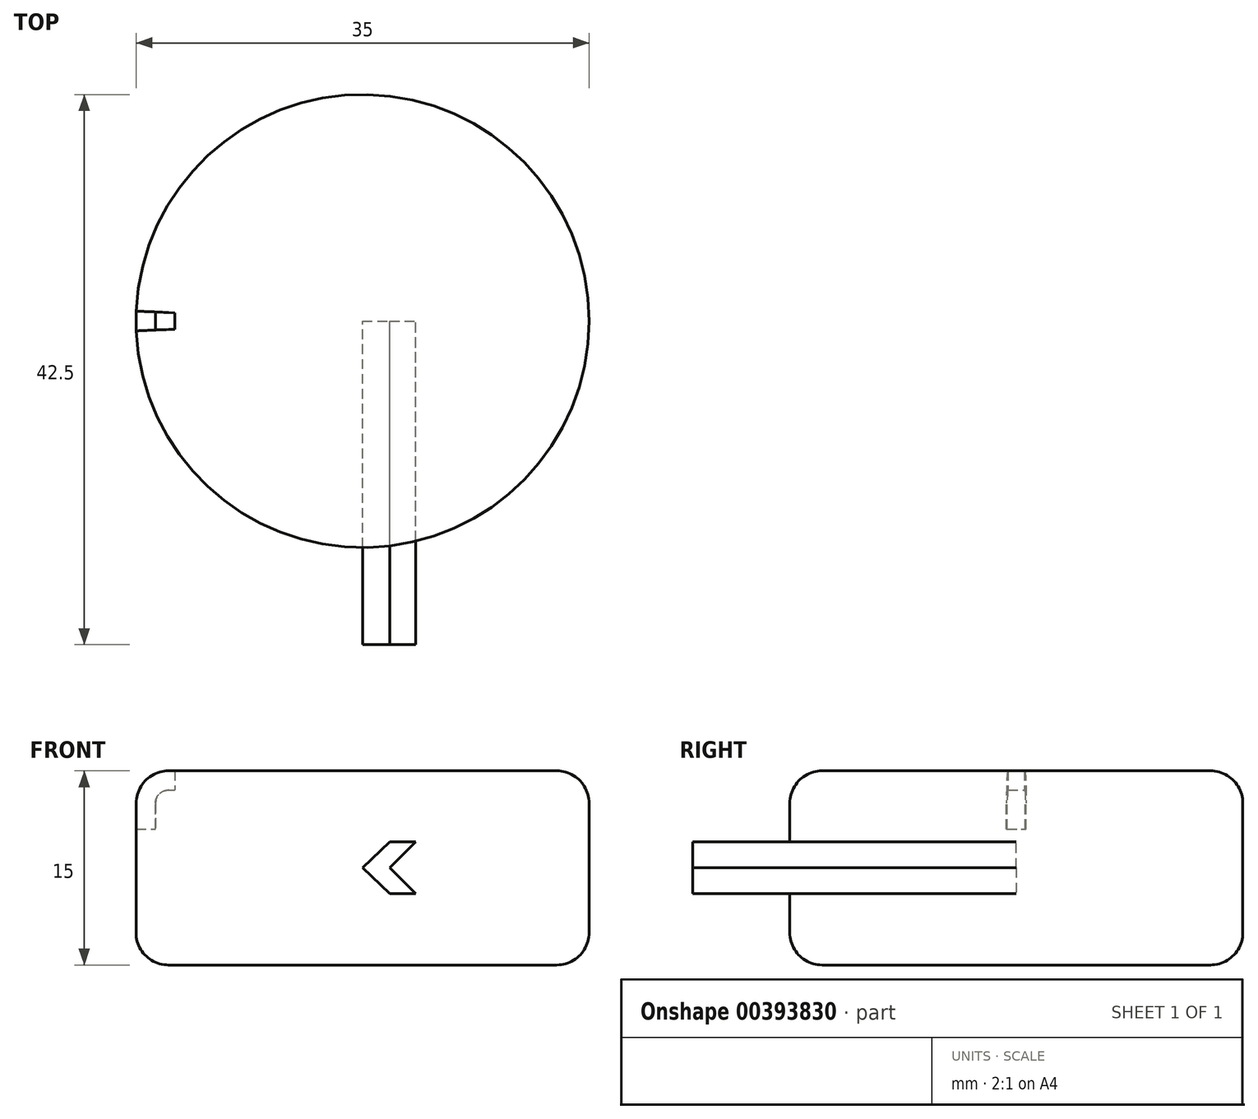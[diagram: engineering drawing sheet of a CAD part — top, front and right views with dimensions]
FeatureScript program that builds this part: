
annotation { "Feature Type Name" : "Feature", "Feature Type Description" : "" }
export const myFeature = defineFeature(function(context is Context, id is Id, definition is map)
    precondition{}
    {
        {
            var Q0;
            Q0=qCreatedBy(makeId("Front.planeOp"),FACE);
            var sketch = newSketch(context, id + "F0", { "sketchPlane" : qUnion([Q0])});
            skLineSegment(sketch, "E0", {"start": v(-38.31, 0) * mm, "end": v(38.96, 0) * mm, "construction": true});
            skLineSegment(sketch, "E1", {"start": v(0, 21.6) * mm, "end": v(0, -24.2) * mm, "construction": true});
            skLineSegment(sketch, "E2.bottom", {"start": v(0, 7.5) * mm, "end": v(-17.5, 7.5) * mm});
            skLineSegment(sketch, "E2.top", {"start": v(0, -7.5) * mm, "end": v(-17.5, -7.5) * mm});
            skLineSegment(sketch, "E2.right", {"start": v(-17.5, 7.5) * mm, "end": v(-17.5, -7.5) * mm});
            skPoint(sketch, "E2.middle", {"position": v(0, 0) * mm});
            skPoint(sketch, "E3.orphan", {"position": v(17.5, 7.5) * mm});
            skPoint(sketch, "E4.orphan", {"position": v(17.5, -7.5) * mm});
            skLineSegment(sketch, "E5", {"start": v(0, 7.5) * mm, "end": v(0, -7.5) * mm});
            skSolve(sketch);
        }
        {
            var Q0;
            Q0=makeQuery(id+"F0.imprint","IMPRINT",FACE,{"disambiguationData":[TD([[makeQuery(id+"F0.imprint","IMPRINT",EDGE,{"derivedFrom":sQuery(id+"F0.wireOp",EDGE,"E2.bottom")}),1.0]])]});
            var Q1;
            Q1=sQuery(id+"F0.wireOp",EDGE,"E5");
            revolve(context, id + "F1", {"entities" : qUnion([Q0]), "axis" : qUnion([Q1]), "revolveType" : RevolveType.FULL});
        }
        {
            var Q0;
            Q0=makeQuery(id+"F1.opRevolve","SWEPT_EDGE",EDGE,{"disambiguationData":[OSD([sQuery(id+"F0.wireOp",EDGE,"E2.bottom"),sQuery(id+"F0.wireOp",EDGE,"E2.right")])]});
            var Q1;
            Q1=makeQuery(id+"F1.opRevolve","SWEPT_EDGE",EDGE,{"disambiguationData":[OSD([sQuery(id+"F0.wireOp",EDGE,"E2.top"),sQuery(id+"F0.wireOp",EDGE,"E2.right")])]});
            fillet(context, id + "F2", {"entities" : qUnion([Q0, Q1]), "radius" : 2.5 * mm, "tangentPropagation" : true, "allowEdgeOverflow" : false});
        }
        {
            var Q0;
            Q0=qCreatedBy(makeId("Front.planeOp"),FACE);
            var sketch = newSketch(context, id + "F3", { "sketchPlane" : qUnion([Q0])});
            skLineSegment(sketch, "E6", {"start": v(-39.64, 0) * mm, "end": v(41.28, 0) * mm, "construction": true});
            skLineSegment(sketch, "E7", {"start": v(0, 20.88) * mm, "end": v(0, -28.83) * mm, "construction": true});
            skLineSegment(sketch, "E8", {"start": v(-15, 7.5) * mm, "end": v(15, 7.5) * mm});
            skArc(sketch, "E9", {"start": v(-15, 7.5) * mm, "mid": v(-16.77, 6.77) * mm, "end": v(-17.5, 5) * mm});
            skArc(sketch, "E10", {"start": v(17.5, 5) * mm, "mid": v(16.77, 6.77) * mm, "end": v(15, 7.5) * mm});
            skLineSegment(sketch, "E11", {"start": v(17.5, 5) * mm, "end": v(17.5, -5) * mm});
            skLineSegment(sketch, "E12", {"start": v(-17.5, -5) * mm, "end": v(-17.5, 5) * mm});
            skLineSegment(sketch, "E13.0", {"start": v(16, 5) * mm, "end": v(16, -5) * mm});
            skLineSegment(sketch, "E13.1", {"start": v(-16, -5) * mm, "end": v(-16, 5) * mm});
            skArc(sketch, "E13.2", {"start": v(-15, 6) * mm, "mid": v(-15.7, 5.7) * mm, "end": v(-16, 5) * mm});
            skLineSegment(sketch, "E13.3", {"start": v(-15, 6) * mm, "end": v(15, 6) * mm});
            skArc(sketch, "E13.4", {"start": v(16, 5) * mm, "mid": v(15.7, 5.7) * mm, "end": v(15, 6) * mm});
            skLineSegment(sketch, "E14", {"start": v(-14.5, 7.5) * mm, "end": v(-14.5, 6) * mm});
            skLineSegment(sketch, "E15", {"start": v(-17.5, 3) * mm, "end": v(-16, 3) * mm});
            skSolve(sketch);
        }
        {
            var Q0;
            Q0 = qSketchRegion(id + "F3", true);
            var Q1;
            Q1=sQuery(id+"F3.wireOp",EDGE,"E7");
            revolve(context, id + "F4", {"operationType" : NewBodyOperationType.REMOVE, "entities" : qUnion([Q0]), "axis" : qUnion([Q1]), "revolveType" : RevolveType.SYMMETRIC, "oppositeDirection" : true, "angle" : 5 * degree});
        }
        {
            var Q0;
            Q0=qCreatedBy(makeId("Front.planeOp"),FACE);
            var sketch = newSketch(context, id + "F5", { "sketchPlane" : qUnion([Q0])});
            skLineSegment(sketch, "E16", {"start": v(-40.58, 0) * mm, "end": v(37.62, 0) * mm, "construction": true});
            skLineSegment(sketch, "E17", {"start": v(0, 0) * mm, "end": v(2.1, 2) * mm});
            skLineSegment(sketch, "E18", {"start": v(2.1, 2) * mm, "end": v(4.1, 2) * mm});
            skLineSegment(sketch, "E19", {"start": v(4.1, 2) * mm, "end": v(2.1, 0) * mm});
            skLineSegment(sketch, "E20", {"start": v(2.1, 0) * mm, "end": v(0, 0) * mm});
            skLineSegment(sketch, "E21.MirrorCS", {"start": v(4.1, -2) * mm, "end": v(2.1, 0) * mm});
            skLineSegment(sketch, "E22.MirrorCS", {"start": v(2.1, -2) * mm, "end": v(4.1, -2) * mm});
            skLineSegment(sketch, "E23.MirrorCS", {"start": v(0, 0) * mm, "end": v(2.1, -2) * mm});
            skSolve(sketch);
        }
        {
            var Q0;
            Q0 = qSketchRegion(id + "F5", true);
            extrude(context, id + "F6", {"entities" : qUnion([Q0]), "depth" : 25 * mm});
        }
    });
